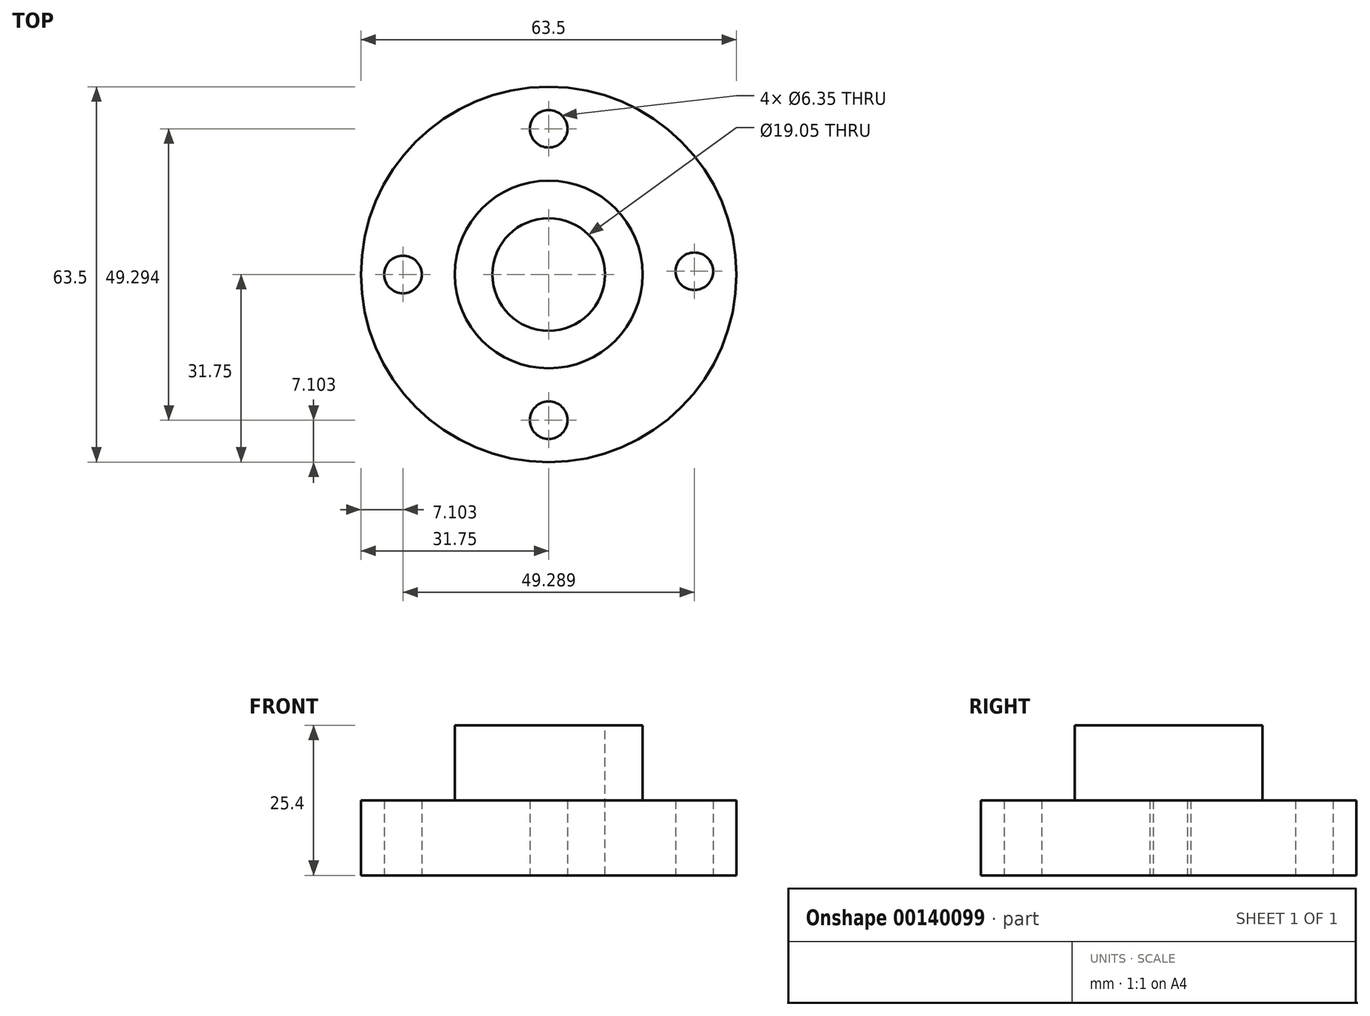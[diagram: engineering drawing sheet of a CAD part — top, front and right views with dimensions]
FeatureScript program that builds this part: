
annotation { "Feature Type Name" : "Feature", "Feature Type Description" : "" }
export const myFeature = defineFeature(function(context is Context, id is Id, definition is map)
    precondition{}
    {
        {
            var Q0;
            Q0=qCreatedBy(makeId("Top.planeOp"),FACE);
            var sketch = newSketch(context, id + "F0", { "sketchPlane" : qUnion([Q0])});
            skCircle(sketch, "E0", {"center": v(0, 0) * mm, "radius": 24.65 * mm});
            skCircle(sketch, "E1", {"center": v(0, 0) * mm, "radius": 31.75 * mm});
            skCircle(sketch, "E2", {"center": v(0, 24.65) * mm, "radius": 3.18 * mm});
            skCircle(sketch, "E3", {"center": v(24.64, 0.53) * mm, "radius": 3.18 * mm});
            skCircle(sketch, "E4", {"center": v(-24.65, 0) * mm, "radius": 3.18 * mm});
            skCircle(sketch, "E5", {"center": v(0, -24.65) * mm, "radius": 3.18 * mm});
            skSolve(sketch);
        }
        {
            var Q0;
            Q0 = qSketchRegion(id + "F0", true);
            extrude(context, id + "F1", {"entities" : qUnion([Q0]), "depth" : 12.7 * mm});
        }
        {
            var Q0;
            Q0=makeQuery(id+"F1.opExtrude","CAP_FACE",FACE,{"disambiguationData":[OSD([sQuery(id+"F0.wireOp",EDGE,"E0"),sQuery(id+"F0.wireOp",EDGE,"E1"),sQuery(id+"F0.wireOp",EDGE,"E2"),sQuery(id+"F0.wireOp",EDGE,"E3"),sQuery(id+"F0.wireOp",EDGE,"E4"),sQuery(id+"F0.wireOp",EDGE,"E5")])],"isStart":false});
            var sketch = newSketch(context, id + "F2", { "sketchPlane" : qUnion([Q0])});
            skArc(sketch, "E6.0", {"start": v(-3.17, 24.44) * mm, "mid": v(-17.43, 17.43) * mm, "end": v(-24.44, 3.17) * mm});
            skArc(sketch, "E7.0", {"start": v(24.37, 3.7) * mm, "mid": v(17.24, 17.62) * mm, "end": v(3.17, 24.44) * mm});
            skArc(sketch, "E8.0", {"start": v(3.17, -24.44) * mm, "mid": v(17.62, -17.24) * mm, "end": v(24.5, -2.64) * mm});
            skArc(sketch, "E9.0", {"start": v(-24.44, -3.17) * mm, "mid": v(-17.43, -17.43) * mm, "end": v(-3.17, -24.44) * mm});
            skArc(sketch, "E10", {"start": v(-24.44, -3.17) * mm, "mid": v(-21.47, 0) * mm, "end": v(-24.44, 3.17) * mm});
            skArc(sketch, "E11", {"start": v(-3.17, 24.44) * mm, "mid": v(0, 21.47) * mm, "end": v(3.17, 24.44) * mm});
            skArc(sketch, "E12", {"start": v(24.37, 3.7) * mm, "mid": v(21.47, 0.47) * mm, "end": v(24.5, -2.64) * mm});
            skArc(sketch, "E13", {"start": v(3.17, -24.44) * mm, "mid": v(0, -21.47) * mm, "end": v(-3.17, -24.44) * mm});
            skSolve(sketch);
        }
        {
            var Q0;
            Q0 = qSketchRegion(id + "F2", true);
            var Q1;
            Q1=makeQuery(id+"F2.imprint","IMPRINT",FACE,{"disambiguationData":[TD([[makeQuery(id+"F2.imprint","IMPRINT",EDGE,{"derivedFrom":sQuery(id+"F2.wireOp",EDGE,"E6.0")}),-1.0]])]});
            extrude(context, id + "F3", {"entities" : qUnion([Q0, Q1]), "operationType" : NewBodyOperationType.ADD, "oppositeDirection" : true, "depth" : 6.35 * mm});
        }
        {
            var Q0;
            Q0=makeQuery(id+"F3.opExtrude","CAP_FACE",FACE,{"disambiguationData":[OSD([sQuery(id+"F0.wireOp",EDGE,"E1"),sQuery(id+"F0.wireOp",EDGE,"E2"),sQuery(id+"F0.wireOp",EDGE,"E3"),sQuery(id+"F0.wireOp",EDGE,"E4"),sQuery(id+"F0.wireOp",EDGE,"E5"),sQuery(id+"F2.wireOp",EDGE,"E10"),sQuery(id+"F2.wireOp",EDGE,"E11"),sQuery(id+"F2.wireOp",EDGE,"E12"),sQuery(id+"F2.wireOp",EDGE,"E13")])],"isStart":false});
            var sketch = newSketch(context, id + "F4", { "sketchPlane" : qUnion([Q0])});
            skSolve(sketch);
        }
        {
            var Q0;
            {var subQ0=sQuery(id+"F0.wireOp",EDGE,"E5");var subQ1=sQuery(id+"F0.wireOp",EDGE,"E4");var subQ2=sQuery(id+"F0.wireOp",EDGE,"E3");var subQ3=sQuery(id+"F0.wireOp",EDGE,"E2");var subQ4=sQuery(id+"F0.wireOp",EDGE,"E1");Q0=makeQuery(id+"F3.boolean.opBoolean","MERGE",FACE,{"derivedFrom":[makeQuery(id+"F1.opExtrude","CAP_FACE",FACE,{"disambiguationData":[OSD([sQuery(id+"F0.wireOp",EDGE,"E0"),subQ4,subQ3,subQ2,subQ1,subQ0])],"isStart":false}),makeQuery(id+"F3.opExtrude","CAP_FACE",FACE,{"disambiguationData":[OSD([subQ4,subQ3,subQ2,subQ1,subQ0,sQuery(id+"F2.wireOp",EDGE,"E10"),sQuery(id+"F2.wireOp",EDGE,"E11"),sQuery(id+"F2.wireOp",EDGE,"E12"),sQuery(id+"F2.wireOp",EDGE,"E13")])],"isStart":true})]});}
            var sketch = newSketch(context, id + "F5", { "sketchPlane" : qUnion([Q0])});
            skCircle(sketch, "E14", {"center": v(0, 0) * mm, "radius": 9.53 * mm});
            skSolve(sketch);
        }
        {
            var Q0;
            Q0 = qSketchRegion(id + "F5", true);
            extrude(context, id + "F6", {"entities" : qUnion([Q0]), "operationType" : NewBodyOperationType.REMOVE, "oppositeDirection" : true, "depth" : 25.4 * mm, "hasSecondDirection" : true, "secondDirectionBound" : SecondDirectionBoundingType.THROUGH_ALL, "secondDirectionOppositeDirection" : false, "secondDirectionDepth" : 25.4 * mm});
        }
        {
            var Q0;
            {var subQ0=sQuery(id+"F0.wireOp",EDGE,"E5");var subQ1=sQuery(id+"F0.wireOp",EDGE,"E4");var subQ2=sQuery(id+"F0.wireOp",EDGE,"E3");var subQ3=sQuery(id+"F0.wireOp",EDGE,"E2");var subQ4=sQuery(id+"F0.wireOp",EDGE,"E1");Q0=makeQuery(id+"F3.boolean.opBoolean","MERGE",FACE,{"derivedFrom":[makeQuery(id+"F1.opExtrude","CAP_FACE",FACE,{"disambiguationData":[OSD([sQuery(id+"F0.wireOp",EDGE,"E0"),subQ4,subQ3,subQ2,subQ1,subQ0])],"isStart":false}),makeQuery(id+"F3.opExtrude","CAP_FACE",FACE,{"disambiguationData":[OSD([subQ4,subQ3,subQ2,subQ1,subQ0,sQuery(id+"F2.wireOp",EDGE,"E10"),sQuery(id+"F2.wireOp",EDGE,"E11"),sQuery(id+"F2.wireOp",EDGE,"E12"),sQuery(id+"F2.wireOp",EDGE,"E13")])],"isStart":true})]});}
            var sketch = newSketch(context, id + "F7", { "sketchPlane" : qUnion([Q0])});
            skCircle(sketch, "E15", {"center": v(0, 0) * mm, "radius": 15.88 * mm});
            skSolve(sketch);
        }
        {
            var Q0;
            Q0 = qSketchRegion(id + "F7", true);
            extrude(context, id + "F8", {"entities" : qUnion([Q0]), "operationType" : NewBodyOperationType.ADD, "depth" : 12.7 * mm});
        }
        {
            var Q0;
            Q0=makeQuery(id+"F8.opExtrude","CAP_FACE",FACE,{"disambiguationData":[OSD([sQuery(id+"F7.wireOp",EDGE,"E15")])],"isStart":false});
            var sketch = newSketch(context, id + "F9", { "sketchPlane" : qUnion([Q0])});
            skCircle(sketch, "E16", {"center": v(0, 0) * mm, "radius": 9.53 * mm});
            skSolve(sketch);
        }
        {
            var Q0;
            Q0 = qSketchRegion(id + "F9", true);
            extrude(context, id + "F10", {"entities" : qUnion([Q0]), "operationType" : NewBodyOperationType.REMOVE, "oppositeDirection" : true, "depth" : 25.4 * mm});
        }
        {
            var Q0;
            {var subQ4=sQuery(id+"F2.wireOp",EDGE,"E10");var subQ5=sQuery(id+"F0.wireOp",EDGE,"E4");Q0=makeQuery(id+"F4.imprint","IMPRINT",FACE,{"disambiguationData":[TD([[makeQuery(id+"F4.imprint","IMPRINT",EDGE,{"derivedFrom":makeQuery(id+"F3.opExtrude","CAP_EDGE",EDGE,{"disambiguationData":[OSD([subQ5,subQ4])],"isStart":false})}),1.0]])]});}
            var sketch = newSketch(context, id + "F11", { "sketchPlane" : qUnion([Q0])});
            skArc(sketch, "E17.0", {"start": v(-24.44, 3.17) * mm, "mid": v(-17.43, 17.43) * mm, "end": v(-3.17, 24.44) * mm});
            skArc(sketch, "E18.0", {"start": v(3.17, 24.44) * mm, "mid": v(0, 21.47) * mm, "end": v(-3.17, 24.44) * mm});
            skArc(sketch, "E19.0", {"start": v(3.17, 24.44) * mm, "mid": v(17.62, 17.24) * mm, "end": v(24.5, 2.64) * mm});
            skArc(sketch, "E20.0", {"start": v(24.37, -3.7) * mm, "mid": v(21.47, -0.47) * mm, "end": v(24.5, 2.64) * mm});
            skArc(sketch, "E21.0", {"start": v(24.37, -3.7) * mm, "mid": v(17.24, -17.62) * mm, "end": v(3.17, -24.44) * mm});
            skArc(sketch, "E22.0", {"start": v(-3.17, -24.44) * mm, "mid": v(0, -21.47) * mm, "end": v(3.17, -24.44) * mm});
            skArc(sketch, "E23.0", {"start": v(-3.17, -24.44) * mm, "mid": v(-17.43, -17.43) * mm, "end": v(-24.44, -3.17) * mm});
            skArc(sketch, "E24.0", {"start": v(-24.44, 3.17) * mm, "mid": v(-21.47, 0) * mm, "end": v(-24.44, -3.17) * mm});
            skCircle(sketch, "E25.0", {"center": v(0, 0) * mm, "radius": 9.53 * mm});
            skSolve(sketch);
        }
        {
            var Q0;
            Q0 = qSketchRegion(id + "F11", true);
            var Q1;
            Q1=makeQuery(id+"F1.opExtrude","CAP_FACE",FACE,{"disambiguationData":[OSD([sQuery(id+"F0.wireOp",EDGE,"E0"),sQuery(id+"F0.wireOp",EDGE,"E1"),sQuery(id+"F0.wireOp",EDGE,"E2"),sQuery(id+"F0.wireOp",EDGE,"E3"),sQuery(id+"F0.wireOp",EDGE,"E4"),sQuery(id+"F0.wireOp",EDGE,"E5")])],"isStart":true});
            extrude(context, id + "F12", {"entities" : qUnion([Q0]), "operationType" : NewBodyOperationType.ADD, "endBound" : BoundingType.UP_TO_SURFACE, "endBoundEntityFace" : qUnion([Q1]), "depth" : 25.4 * mm});
        }
    });
